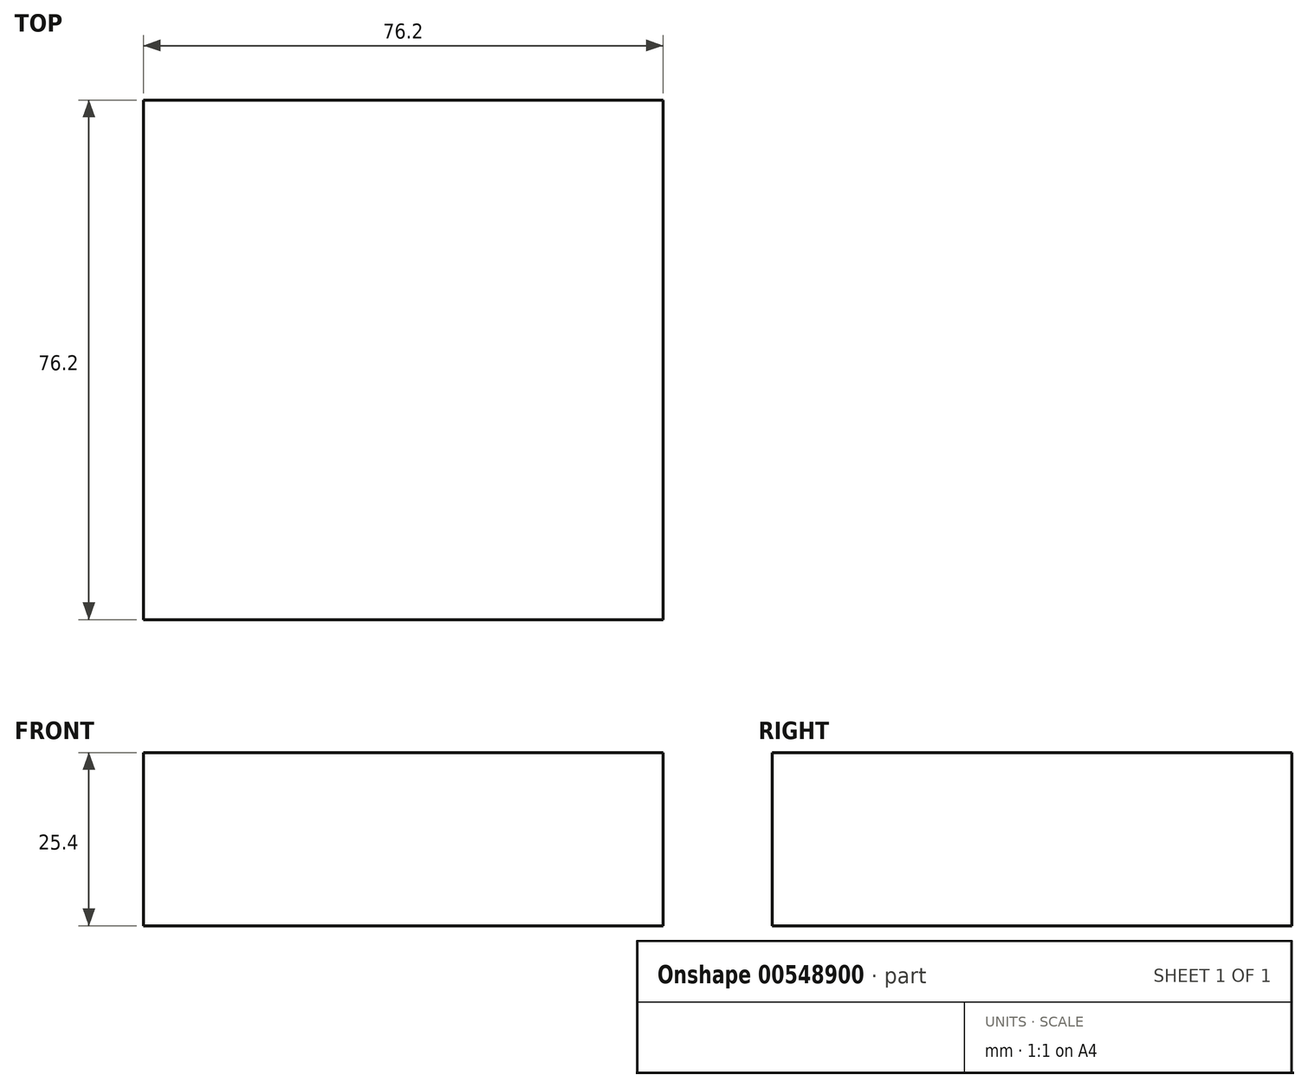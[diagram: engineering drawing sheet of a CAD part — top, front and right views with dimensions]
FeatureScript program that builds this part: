
annotation { "Feature Type Name" : "Feature", "Feature Type Description" : "" }
export const myFeature = defineFeature(function(context is Context, id is Id, definition is map)
    precondition{}
    {
        {
            var Q0;
            Q0=qCreatedBy(makeId("Top.planeOp"),FACE);
            var sketch = newSketch(context, id + "F0", { "sketchPlane" : qUnion([Q0])});
            skLineSegment(sketch, "E0.bottom", {"start": v(38.1, 38.1) * mm, "end": v(-38.1, 38.1) * mm});
            skLineSegment(sketch, "E0.top", {"start": v(38.1, -38.1) * mm, "end": v(-38.1, -38.1) * mm});
            skLineSegment(sketch, "E0.left", {"start": v(38.1, 38.1) * mm, "end": v(38.1, -38.1) * mm});
            skLineSegment(sketch, "E0.right", {"start": v(-38.1, 38.1) * mm, "end": v(-38.1, -38.1) * mm});
            skPoint(sketch, "E0.middle", {"position": v(0, 0) * mm});
            skSolve(sketch);
        }
        {
            var Q0;
            Q0 = qSketchRegion(id + "F0", true);
            extrude(context, id + "F1", {"entities" : qUnion([Q0]), "depth" : 25.4 * mm, "offsetDistance" : 25.4 * mm});
        }
    });
